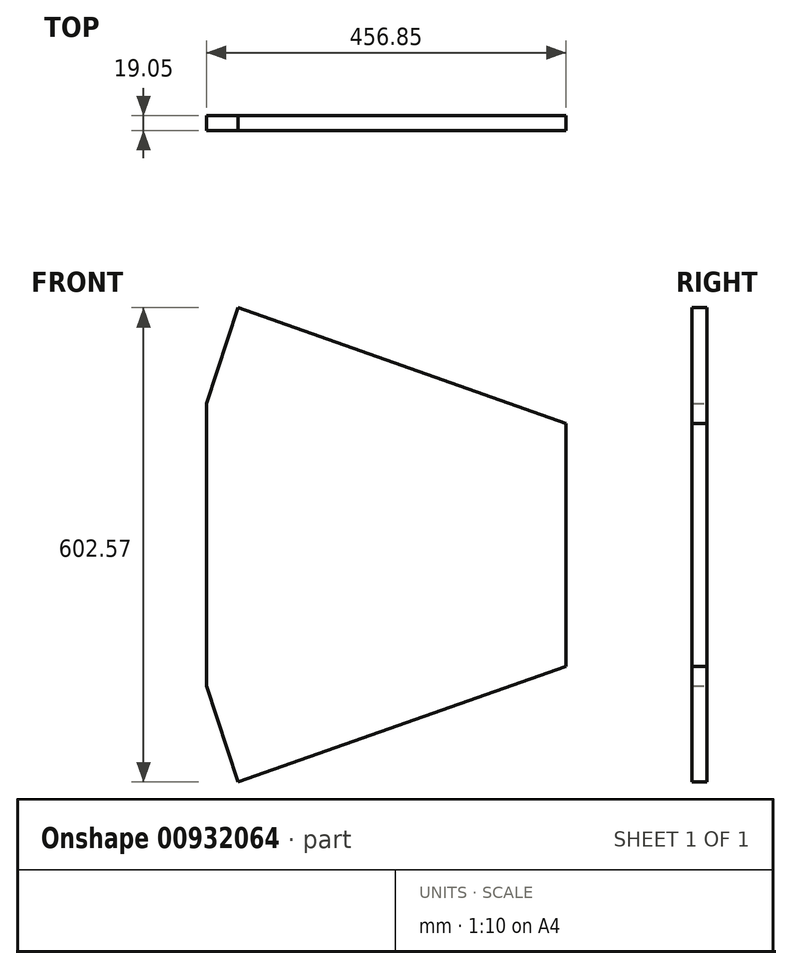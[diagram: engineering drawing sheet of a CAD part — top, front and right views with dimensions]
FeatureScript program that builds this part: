
annotation { "Feature Type Name" : "Feature", "Feature Type Description" : "" }
export const myFeature = defineFeature(function(context is Context, id is Id, definition is map)
    precondition{}
    {
        {
            var Q0;
            Q0=qCreatedBy(makeId("Front.planeOp"),FACE);
            var sketch = newSketch(context, id + "F0", { "sketchPlane" : qUnion([Q0])});
            skLineSegment(sketch, "E0", {"start": v(-131.98, -228.6) * mm, "end": v(263.96, 0) * mm, "construction": true});
            skLineSegment(sketch, "E1", {"start": v(263.96, 0) * mm, "end": v(-131.98, 228.6) * mm, "construction": true});
            skLineSegment(sketch, "E2", {"start": v(-131.98, -228.6) * mm, "end": v(0, 0) * mm, "construction": true});
            skLineSegment(sketch, "E3", {"start": v(0, 0) * mm, "end": v(-131.98, 228.6) * mm, "construction": true});
            skLineSegment(sketch, "E4", {"start": v(0, 0) * mm, "end": v(263.96, 0) * mm, "construction": true});
            skCircle(sketch, "E5", {"center": v(-131.98, 228.6) * mm, "radius": 12.7 * mm, "construction": true});
            skCircle(sketch, "E6", {"center": v(-131.98, -228.6) * mm, "radius": 12.7 * mm, "construction": true});
            skCircle(sketch, "E7", {"center": v(263.96, 0) * mm, "radius": 12.7 * mm, "construction": true});
            skLineSegment(sketch, "E8", {"start": v(-131.98, 228.6) * mm, "end": v(-131.98, 0) * mm, "construction": true});
            skLineSegment(sketch, "E9", {"start": v(-131.98, 0) * mm, "end": v(-131.98, -228.6) * mm, "construction": true});
            skLineSegment(sketch, "E10", {"start": v(-148.02, 179.94) * mm, "end": v(-107.86, 301.8) * mm, "construction": true});
            skLineSegment(sketch, "E11", {"start": v(-148.02, -179.94) * mm, "end": v(-107.86, -301.79) * mm, "construction": true});
            skLineSegment(sketch, "E12", {"start": v(-106.43, -301.28) * mm, "end": v(310.27, -154.25) * mm});
            skLineSegment(sketch, "E13", {"start": v(310.27, -154.25) * mm, "end": v(310.27, 154.25) * mm});
            skLineSegment(sketch, "E14", {"start": v(310.27, 154.25) * mm, "end": v(-106.43, 301.29) * mm});
            skPoint(sketch, "E15", {"position": v(310.27, 0) * mm});
            skPoint(sketch, "E16", {"position": v(-183.84, 0) * mm});
            skLineSegment(sketch, "E17", {"start": v(-106.43, 301.29) * mm, "end": v(-144.8, 184.89) * mm});
            skLineSegment(sketch, "E18", {"start": v(-106.43, -301.28) * mm, "end": v(-144.8, -184.89) * mm});
            skPoint(sketch, "E19.orphan", {"position": v(-183.84, 152.4) * mm});
            skPoint(sketch, "E20.start.orphan", {"position": v(-183.84, -152.4) * mm});
            skLineSegment(sketch, "E21", {"start": v(-144.8, 184.89) * mm, "end": v(-146.58, 179.46) * mm});
            skLineSegment(sketch, "E22", {"start": v(-146.58, 179.46) * mm, "end": v(-146.58, -179.46) * mm});
            skLineSegment(sketch, "E23", {"start": v(-144.8, -184.89) * mm, "end": v(-146.58, -179.46) * mm});
            skSolve(sketch);
        }
        {
            var Q0;
            Q0 = qSketchRegion(id + "F0", true);
            extrude(context, id + "F1", {"entities" : qUnion([Q0]), "depth" : 19.05 * mm, "offsetDistance" : 25.4 * mm});
        }
    });
